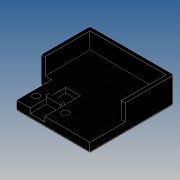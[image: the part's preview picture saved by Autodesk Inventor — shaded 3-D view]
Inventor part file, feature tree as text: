
AUTODESK INVENTOR PART (.ipt)
format: ipt  version: 2016 (Build 200138000, 138)  size: 156,160 bytes
history: native  units: mm
features: extrude x6, sketch x6, fillet x2, hole x1
ambient origin geometry x8: Origin, YZ Plane, XZ Plane, XY Plane, X Axis, Y Axis, Z Axis, Center Point
bodies: Solid1 (feature_tree)
feature tree (15):
  extrude  "Extrusion1"  Depth=43.0mm
  extrude  "Extrusion2"  Depth=2.0mm
  extrude  "Extrusion3"  Depth=8.5mm TaperAngle=0.0deg
  extrude  "Extrusion4"  Depth=25.0mm
  sketch  "Sketch5"  dims[d10=13.5mm d11=0.0mm d12=5.4mm]
  extrude  "Extrusion5"  Depth=5.4mm
  extrude  "Extrusion6"  Depth=7.0mm
  fillet  "Fillet1"  Radius=7.5mm
  fillet  "Fillet2"  Radius=18.2mm
  hole  "Hole1"  [1 undecoded]
  sketch  "Sketch1"  dims[d0=43.0mm d1=43.0mm]
  sketch  "Sketch2"  dims[d2=13.5mm d3=0.0mm d4=2.0mm]
  sketch  "Sketch3"  dims[d5=2.0mm d6=8.5mm d7=0.0mm]
  sketch  "Sketch4"  dims[d8=18.0mm d9=25.0mm]
  sketch  "Sketch6"  dims[d13=13.5mm d14=0.0mm d15=7.0mm d16=7.5mm d17=18.2mm d18=15.0mm d19=6.8mm d20=2.5mm d21=0.0mm d22=1.8mm d23=4.2mm d24=0.0mm d25=0.8mm d26=3.4mm d27=6.0mm d28=6.3mm d29=2.0mm d30=90.0deg d31=8.0mm d32=20.594885mm]
note: 1 required parameter value undecoded (feature->parameter linkage not recoverable at this tier; creation-order binding heuristic only, values carry confidence <= 0.55)
